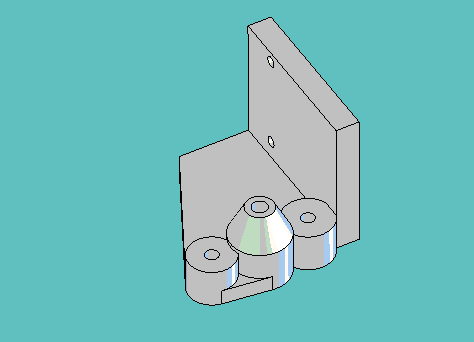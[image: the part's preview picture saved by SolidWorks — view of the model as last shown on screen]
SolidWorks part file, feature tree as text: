
SOLIDWORKS PART (.sldprt)
format: sldprt  version: not decoded by parser v0  size: 417,280 bytes
history: native  units: mm
features: sketch x7, extrude x4, cut_extrude x3, material x1, chamfer x1 (+11 scaffold rows collapsed)
feature tree (27):
  scaffold x11  (default folders/planes/origin — collapsed)
  material  "Material <not specified>"
  sketch  "Sketch1"  dims[c1.D1=12.7mm c1.D2=3.175mm c1.D3=~3.96875mm c1.D5=9.525mm c1.D9=3.175mm c1.D4=9.525mm c1.D6=38.1mm c1.D7=~3.96875mm c1.D8=~15.238942mm c2.D9=~28.332726mm c2.D1=~37.29237mm c3.D1=6.0deg c3.D10=~19.84248mm c3.D4=9.525mm c3.D11=~0.39708mm c3.D8=15.24mm c4.D11=~0.396875mm c4.D4=~9.92124mm c4.D8=7.9375mm c5.D11=~24.60625mm c5.D12=14.2875mm]
  extrude  "Extrude1"  Depth=3.175mm
  sketch  "Sketch2"  dims[D1=~10.31875mm]
  extrude  "Extrude2"  Depth=3.048mm
  sketch  "Sketch3"  dims[D1=12.7mm]
  extrude  "Extrude3"  Depth=11.938mm
  sketch  "Sketch4"
  extrude  "Extrude4"  Depth=26.9875mm
  chamfer  "Chamfer1"  Distance=6.35mm
  sketch  "Sketch5"
  cut_extrude  "Cut-Extrude1"  [1 undecoded]
  sketch  "Sketch6"
  cut_extrude  "Cut-Extrude2"  [1 undecoded]
  sketch  "Sketch7"  dims[D1=2.159mm D2=2.159mm D3=~21.843876mm D4=19.558mm D5=6.9088mm]
  cut_extrude  "Cut-Extrude3"  [1 undecoded]
decode coverage: 9 of 15 modeling features carry decoded parameters
note: ~ marks probable driven/reference dimensions
note: 3 parameter values undecoded
summary: no parameter record found for 3 features
note: suppression state not decoded; provenance and decode notes live in map.json
